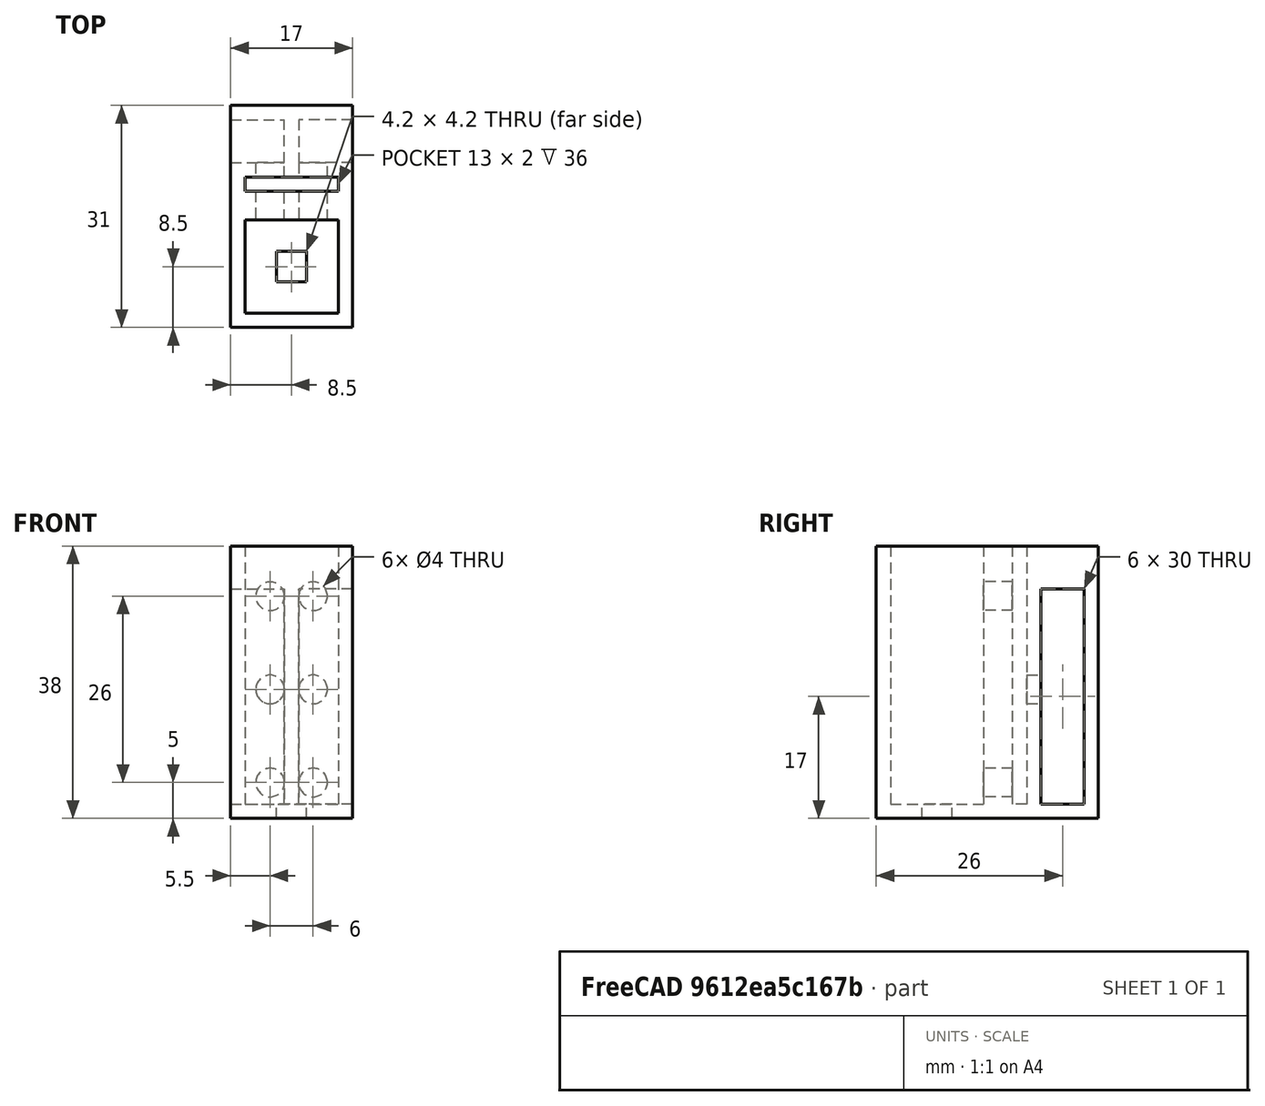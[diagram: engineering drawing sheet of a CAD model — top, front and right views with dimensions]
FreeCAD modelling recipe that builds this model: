
FCSTD DOCUMENT  (FreeCAD 0.18.1R)
Label: CYLINDER
License: All rights reserved
LicenseURL: http://en.wikipedia.org/wiki/All_rights_reserved
objects: TechDraw::DrawViewDimension×12, Sketcher::SketchObject×9, PartDesign::Pocket×7, PartDesign::Plane×6, TechDraw::DrawProjGroupItem×4, TechDraw::DrawSVGTemplate×2, TechDraw::DrawPage×2, PartDesign::Pad×1, PartDesign::Body×1, TechDraw::DrawViewPart×1, TechDraw::DrawProjGroup×1
note: 32 computed .brp shape members not serialized (recipe doc carries the construction recipe); baked Part::Feature solids carry a one-line shape summary decoded from their .brp

FEATURE [Sketcher::SketchObject] Sketch
  MapMode = 5
  Support = -> [XY_Plane]
  sketch-geometry (4):
    g0: LineSegment StartX=0 StartY=31 StartZ=0 EndX=17 EndY=31 EndZ=0
    g1: LineSegment StartX=17 StartY=31 StartZ=0 EndX=17 EndY=0 EndZ=0
    g2: LineSegment StartX=17 StartY=0 StartZ=0 EndX=0 EndY=0 EndZ=0
    g3: LineSegment StartX=0 StartY=0 StartZ=0 EndX=0 EndY=31 EndZ=0
  constraints (11):
    c: Coincident(g0,g1)
    c: Coincident(g1,g2)
    c: Coincident(g2,g3)
    c: Coincident(g3,g0)
    c: Horizontal(g0)
    c: Horizontal(g2)
    c: Vertical(g1)
    c: Vertical(g3)
    c: Coincident(g2,g-1)
    c: DistanceX(g2,g2) = 17
    c: DistanceY(g3,g3) = 31
FEATURE [PartDesign::Pad] Pad
  Length = 38
  Length2 = 100
  Profile = -> Sketch
  Type = 0
FEATURE [PartDesign::Plane] DatumPlane
  Length = 33.6543
  MapMode = 5
  Placement = pos=(0,0,38) rot=(0,0,1;0rad)
  ResizeMode = 0
  Support = -> [Pad]
  Width = 47.6543
FEATURE [Sketcher::SketchObject] Sketch001
  MapMode = 5
  Placement = pos=(0,0,38) rot=(0,0,1;0rad)
  Support = -> [DatumPlane]
  sketch-geometry (4):
    g0: LineSegment StartX=2 StartY=21 StartZ=0 EndX=15 EndY=21 EndZ=0
    g1: LineSegment StartX=15 StartY=21 StartZ=0 EndX=15 EndY=19 EndZ=0
    g2: LineSegment StartX=15 StartY=19 StartZ=0 EndX=2 EndY=19 EndZ=0
    g3: LineSegment StartX=2 StartY=19 StartZ=0 EndX=2 EndY=21 EndZ=0
  constraints (12):
    c: Coincident(g0,g1)
    c: Coincident(g1,g2)
    c: Coincident(g2,g3)
    c: Coincident(g3,g0)
    c: Horizontal(g0)
    c: Horizontal(g2)
    c: Vertical(g1)
    c: Vertical(g3)
    c: DistanceX(g0,g0) = 13
    c: DistanceY(g1,g1) = 2
    c: DistanceX(g-1,g2) = 2
    c: DistanceY(g-1,g0) = 21
FEATURE [Sketcher::SketchObject] Sketch002
  MapMode = 5
  Placement = pos=(0,0,38) rot=(0,0,1;0rad)
  Support = -> [DatumPlane]
  sketch-geometry (4):
    g0: LineSegment StartX=2 StartY=15 StartZ=0 EndX=15 EndY=15 EndZ=0
    g1: LineSegment StartX=15 StartY=15 StartZ=0 EndX=15 EndY=2 EndZ=0
    g2: LineSegment StartX=15 StartY=2 StartZ=0 EndX=2 EndY=2 EndZ=0
    g3: LineSegment StartX=2 StartY=2 StartZ=0 EndX=2 EndY=15 EndZ=0
  constraints (12):
    c: Coincident(g0,g1)
    c: Coincident(g1,g2)
    c: Coincident(g2,g3)
    c: Coincident(g3,g0)
    c: Horizontal(g0)
    c: Horizontal(g2)
    c: Vertical(g1)
    c: Vertical(g3)
    c: DistanceX(g0,g0) = 13
    c: DistanceY(g1,g1) = 13
    c: DistanceX(g-1,g2) = 2
    c: DistanceY(g-1,g0) = 15
FEATURE [PartDesign::Pocket] Pocket001
  BaseFeature = -> Pad
  Length = 36
  Length2 = 100
  Profile = -> Sketch002
  Type = 0
FEATURE [PartDesign::Plane] DatumPlane001
  Length = 33.6543
  MapMode = 5
  Placement = pos=(0,0,0) rot=(1,0,0;3.14159rad)
  ResizeMode = 0
  Support = -> [Pocket001]
  Width = 47.6543
FEATURE [Sketcher::SketchObject] Sketch003
  MapMode = 5
  Placement = pos=(0,0,0) rot=(1,0,0;3.14159rad)
  Support = -> [DatumPlane001]
  sketch-geometry (4):
    g0: LineSegment StartX=6.4 StartY=-6.4 StartZ=0 EndX=10.6 EndY=-6.4 EndZ=0
    g1: LineSegment StartX=10.6 StartY=-6.4 StartZ=0 EndX=10.6 EndY=-10.6 EndZ=0
    g2: LineSegment StartX=10.6 StartY=-10.6 StartZ=0 EndX=6.4 EndY=-10.6 EndZ=0
    g3: LineSegment StartX=6.4 StartY=-10.6 StartZ=0 EndX=6.4 EndY=-6.4 EndZ=0
  constraints (12):
    c: Coincident(g0,g1)
    c: Coincident(g1,g2)
    c: Coincident(g2,g3)
    c: Coincident(g3,g0)
    c: Horizontal(g0)
    c: Horizontal(g2)
    c: Vertical(g1)
    c: Vertical(g3)
    c: DistanceX(g0,g0) = 4.2
    c: Equal(g0,g3)
    c: DistanceY(g0,g-1) = 6.4
    c: DistanceX(g-1,g0) = 6.4
FEATURE [PartDesign::Pocket] Pocket002
  BaseFeature = -> Pocket001
  Length = 5
  Length2 = 100
  Profile = -> Sketch003
  Type = 0
FEATURE [PartDesign::Pocket] Pocket
  BaseFeature = -> Pocket002
  Length = 36
  Length2 = 100
  Profile = -> Sketch001
  Type = 0
FEATURE [PartDesign::Plane] DatumPlane002
  Length = 49.8724
  MapMode = 5
  Placement = pos=(0,0,0) rot=(0.57735,-0.57735,-0.57735;2.0944rad)
  ResizeMode = 0
  Support = -> [Pocket]
  Width = 56.8724
FEATURE [Sketcher::SketchObject] Sketch004
  MapMode = 5
  Placement = pos=(0,0,0) rot=(0.57735,-0.57735,-0.57735;2.0944rad)
  Support = -> [DatumPlane002]
  sketch-geometry (4):
    g0: LineSegment StartX=-29 StartY=32 StartZ=0 EndX=-23 EndY=32 EndZ=0
    g1: LineSegment StartX=-23 StartY=32 StartZ=0 EndX=-23 EndY=2 EndZ=0
    g2: LineSegment StartX=-23 StartY=2 StartZ=0 EndX=-29 EndY=2 EndZ=0
    g3: LineSegment StartX=-29 StartY=2 StartZ=0 EndX=-29 EndY=32 EndZ=0
  constraints (12):
    c: Coincident(g0,g1)
    c: Coincident(g1,g2)
    c: Coincident(g2,g3)
    c: Coincident(g3,g0)
    c: Horizontal(g0)
    c: Horizontal(g2)
    c: Vertical(g1)
    c: Vertical(g3)
    c: DistanceY(g3,g3) = 30
    c: DistanceX(g0,g0) = 6
    c: DistanceX(g1,g-1) = 23
    c: DistanceY(g-1,g2) = 2
FEATURE [Sketcher::SketchObject] Sketch005
  MapMode = 5
  Placement = pos=(0,0,0) rot=(0.57735,-0.57735,-0.57735;2.0944rad)
  Support = -> [DatumPlane002]
FEATURE [PartDesign::Pocket] Pocket003
  BaseFeature = -> Pocket
  Length = 7.5
  Length2 = 100
  Profile = -> Sketch004
  Type = 0
FEATURE [PartDesign::Plane] DatumPlane003
  Length = 49.8724
  MapMode = 5
  Placement = pos=(17,0,0) rot=(0.57735,0.57735,0.57735;2.0944rad)
  ResizeMode = 0
  Support = -> [Pocket003]
  Width = 56.8724
FEATURE [Sketcher::SketchObject] Sketch006
  MapMode = 5
  Placement = pos=(17,0,0) rot=(0.57735,0.57735,0.57735;2.0944rad)
  Support = -> [DatumPlane003]
  sketch-geometry (4):
    g0: LineSegment StartX=23 StartY=32 StartZ=0 EndX=29 EndY=32 EndZ=0
    g1: LineSegment StartX=29 StartY=32 StartZ=0 EndX=29 EndY=2 EndZ=0
    g2: LineSegment StartX=29 StartY=2 StartZ=0 EndX=23 EndY=2 EndZ=0
    g3: LineSegment StartX=23 StartY=2 StartZ=0 EndX=23 EndY=32 EndZ=0
  constraints (12):
    c: Coincident(g0,g1)
    c: Coincident(g1,g2)
    c: Coincident(g2,g3)
    c: Coincident(g3,g0)
    c: Horizontal(g0)
    c: Horizontal(g2)
    c: Vertical(g1)
    c: Vertical(g3)
    c: DistanceY(g1,g1) = 30
    c: DistanceX(g2,g2) = 6
    c: DistanceX(g-1,g2) = 23
    c: DistanceY(g-1,g2) = 2
FEATURE [PartDesign::Pocket] Pocket004
  BaseFeature = -> Pocket003
  Length = 7.5
  Length2 = 100
  Profile = -> Sketch006
  Type = 0
FEATURE [PartDesign::Plane] DatumPlane004
  Length = 34.2
  MapMode = 5
  Placement = pos=(0,15,0) rot=(1,0,0;1.5708rad)
  ResizeMode = 0
  Support = -> [Pocket004]
  Width = 55.2
FEATURE [Sketcher::SketchObject] Sketch007
  MapMode = 5
  Placement = pos=(0,15,0) rot=(1,0,0;1.5708rad)
  Support = -> [DatumPlane004]
  sketch-geometry (4):
    g0: Circle CenterX=5.5 CenterY=31 CenterZ=0 NormalX=0 NormalY=0 NormalZ=1 AngleXU=0 Radius=2
    g1: Circle CenterX=11.5 CenterY=31 CenterZ=0 NormalX=0 NormalY=0 NormalZ=1 AngleXU=0 Radius=2
    g2: Circle CenterX=5.5 CenterY=5 CenterZ=0 NormalX=0 NormalY=0 NormalZ=1 AngleXU=0 Radius=2
    g3: Circle CenterX=11.5 CenterY=5 CenterZ=0 NormalX=0 NormalY=0 NormalZ=1 AngleXU=0 Radius=2
  constraints (12):
    c: Radius(g0) = 2
    c: Radius(g1) = 2
    c: Radius(g2) = 2
    c: Radius(g3) = 2
    c: DistanceX(g0,g1) = 6
    c: DistanceY(g1,g0) = 0
    c: DistanceX(g2,g3) = 6
    c: DistanceY(g3,g2) = 0
    c: DistanceY(g2,g0) = 26
    c: DistanceX(g0,g2) = 0
    c: DistanceY(g-1,g0) = 31
    c: DistanceX(g2,g-1) = -5.5
FEATURE [PartDesign::Pocket] Pocket005
  BaseFeature = -> Pocket004
  Length = 5
  Length2 = 100
  Profile = -> Sketch007
  Type = 0
FEATURE [PartDesign::Plane] DatumPlane005
  Length = 34.2
  MapMode = 5
  Placement = pos=(0,23,0) rot=(0,0.707107,0.707107;3.14159rad)
  ResizeMode = 0
  Support = -> [Pocket005]
  Width = 55.2
FEATURE [Sketcher::SketchObject] Sketch008
  MapMode = 5
  Placement = pos=(0,23,0) rot=(0,0.707107,0.707107;3.14159rad)
  Support = -> [DatumPlane005]
  sketch-geometry (2):
    g0: Circle CenterX=-5.5 CenterY=18 CenterZ=0 NormalX=0 NormalY=0 NormalZ=1 AngleXU=0 Radius=2
    g1: Circle CenterX=-11.5 CenterY=18 CenterZ=0 NormalX=0 NormalY=0 NormalZ=1 AngleXU=0 Radius=2
  constraints (6):
    c: Radius(g0) = 2
    c: Radius(g1) = 2
    c: DistanceX(g1,g0) = 6
    c: DistanceY(g1,g0) = 0
    c: DistanceY(g-1,g1) = 18
    c: DistanceX(g-1,g0) = -5.5
FEATURE [PartDesign::Pocket] Pocket006
  BaseFeature = -> Pocket005
  Length = 2
  Length2 = 100
  Profile = -> Sketch008
  Type = 0
FEATURE [PartDesign::Body] Body
  Group = -> [Sketch,Pad,DatumPlane,Sketch001,Sketch002,Pocket001,DatumPlane001,Sketch003,Pocket002,Pocket,DatumPlane002,Sketch004,Sketch005,Pocket003,DatumPlane003,Sketch006,Pocket004,DatumPlane004,Sketch007,Pocket005,DatumPlane005,Sketch008,Pocket006]
  Origin = -> Origin
  Tip = -> Pocket006
FEATURE [TechDraw::DrawSVGTemplate] Template
  EditableTexts = Designed_by_Name=Designed by Name; Drawing_number=Drawing number; FC-Date=Date; FC-SC=Scale; FC-SH=Sheet; FC-Title=Title; Subtitle=Subtitle; Weight=Weight
  Height = 210
  Orientation = 1
  Width = 297
FEATURE [TechDraw::DrawViewPart] View
  CoarseView = false
  Direction = (0,-1,0)
  Focus = 100
  HardHidden = false
  IsoCount = 0
  IsoHidden = false
  IsoVisible = false
  LockPosition = false
  Perspective = false
  Rotation = 0
  ScaleType = 0
  SeamHidden = false
  SeamVisible = false
  SmoothHidden = false
  SmoothVisible = false
  Source = -> [Body]
  X = 148.5
  Y = 105
FEATURE [TechDraw::DrawPage] Page
  KeepUpdated = true
  ProjectionType = 0
  Template = -> Template
  Views = -> [View]
FEATURE [TechDraw::DrawSVGTemplate] Template001
  EditableTexts = Approved1=Approved 1; Approved2=Approved 2; CheckedBy=Checked By; Code=Code; CompanyAddress=1234 Main St; CompanyName=Company Name; DrawingNumber=Drawing Number; DrawingTitle1=CYLINDER; DrawnBy=Drawn By; Revision=Rev; Scale=Scale; Sheet=Sheet n of m; Weight=Weight
  Height = 279.4
  Orientation = 1
  Width = 431.8
FEATURE [TechDraw::DrawProjGroupItem] ProjItem  label="Front"
  CoarseView = false
  Direction = (0,-1,0)
  Focus = 100
  HardHidden = false
  IsoCount = 0
  IsoHidden = false
  IsoVisible = false
  LockPosition = true
  Perspective = false
  Rotation = 0
  RotationVector = (1,0,0)
  Scale = 2
  ScaleType = 2
  SeamHidden = false
  SeamVisible = false
  SmoothHidden = false
  SmoothVisible = false
  Source = -> [Body]
  Type = 0
  X = 0
  Y = 0
FEATURE [TechDraw::DrawProjGroupItem] ProjItem001  label="Left"
  CoarseView = false
  Direction = (-1,-1e-16,0)
  Focus = 100
  HardHidden = false
  IsoCount = 0
  IsoHidden = false
  IsoVisible = false
  LockPosition = false
  Perspective = false
  Rotation = 0
  RotationVector = (1e-16,-1,0)
  Scale = 2
  ScaleType = 2
  SeamHidden = false
  SeamVisible = false
  SmoothHidden = false
  SmoothVisible = false
  Source = -> [Body]
  Type = 1
  X = 116.246
  Y = 0
FEATURE [TechDraw::DrawProjGroupItem] ProjItem002  label="FrontTopLeft"
  CoarseView = false
  Direction = (-1,-1,1)
  Focus = 100
  HardHidden = false
  IsoCount = 0
  IsoHidden = false
  IsoVisible = false
  LockPosition = false
  Perspective = false
  Rotation = 0
  RotationVector = (1,-1,0)
  Scale = 2
  ScaleType = 2
  SeamHidden = false
  SeamVisible = false
  SmoothHidden = false
  SmoothVisible = false
  Source = -> [Body]
  Type = 6
  X = 116.246
  Y = -116.246
FEATURE [TechDraw::DrawProjGroupItem] ProjItem003  label="Top"
  CoarseView = false
  Direction = (0,0,1)
  Focus = 100
  HardHidden = false
  IsoCount = 0
  IsoHidden = false
  IsoVisible = false
  LockPosition = false
  Perspective = false
  Rotation = 0
  RotationVector = (1,0,0)
  Scale = 2
  ScaleType = 2
  SeamHidden = false
  SeamVisible = false
  SmoothHidden = false
  SmoothVisible = false
  Source = -> [Body]
  Type = 4
  X = 0
  Y = -116.246
FEATURE [TechDraw::DrawProjGroup] ProjGroup
  Anchor = -> ProjItem
  AutoDistribute = true
  LockPosition = false
  ProjectionType = 0
  Rotation = 0
  Scale = 2
  ScaleType = 2
  Source = -> [Body]
  Views = -> [ProjItem,ProjItem001,ProjItem002,ProjItem003]
  X = 83.5356
  Y = 201.47
  spacingX = 15
  spacingY = 15
FEATURE [TechDraw::DrawViewDimension] Dimension
  Arbitrary = false
  FormatSpec = %.4f
  LockPosition = false
  MeasureType = 1
  OverTolerance = 0
  References2D = -> [ProjItem]
  Rotation = 0
  ScaleType = 0
  Type = 1
  UnderTolerance = 0
  X = 2.23762
  Y = 48.2931
FEATURE [TechDraw::DrawViewDimension] Dimension001
  Arbitrary = false
  FormatSpec = %.4f
  LockPosition = false
  MeasureType = 1
  OverTolerance = 0
  References2D = -> [ProjItem]
  Rotation = 0
  ScaleType = 0
  Type = 2
  UnderTolerance = 0
  X = -34.0059
  Y = 2.23762
FEATURE [TechDraw::DrawViewDimension] Dimension002
  Arbitrary = false
  FormatSpec = %.4f
  LockPosition = false
  MeasureType = 1
  OverTolerance = 0
  References2D = -> [ProjItem001]
  Rotation = 0
  ScaleType = 0
  Type = 1
  UnderTolerance = 0
  X = 0.447524
  Y = 47.398
FEATURE [TechDraw::DrawViewDimension] Dimension003
  Arbitrary = false
  FormatSpec = %.4f
  LockPosition = false
  MeasureType = 1
  OverTolerance = 0
  References2D = -> [ProjItem001]
  Rotation = 0
  ScaleType = 0
  Type = 2
  UnderTolerance = 0
  X = 43.0832
  Y = 0
FEATURE [TechDraw::DrawViewDimension] Dimension004
  Arbitrary = false
  FormatSpec = %.4f
  LockPosition = false
  MeasureType = 1
  OverTolerance = 0
  References2D = -> [ProjItem001]
  Rotation = 0
  ScaleType = 0
  Type = 1
  UnderTolerance = 0
  X = -18.3149
  Y = 33.6079
FEATURE [TechDraw::DrawViewDimension] Dimension005
  Arbitrary = false
  FormatSpec = %.4f
  LockPosition = false
  MeasureType = 1
  OverTolerance = 0
  References2D = -> [ProjItem001]
  Rotation = 0
  ScaleType = 0
  Type = 2
  UnderTolerance = 0
  X = -9.62971
  Y = -4.89505
FEATURE [TechDraw::DrawViewDimension] Dimension006
  Arbitrary = false
  FormatSpec = %.4f
  LockPosition = false
  MeasureType = 1
  OverTolerance = 0
  References2D = -> [ProjItem003]
  Rotation = 0
  ScaleType = 0
  Type = 1
  UnderTolerance = 0
  X = -1.7901
  Y = 47.1109
FEATURE [TechDraw::DrawViewDimension] Dimension007
  Arbitrary = false
  FormatSpec = %.4f
  LockPosition = false
  MeasureType = 1
  OverTolerance = 0
  References2D = -> [ProjItem003]
  Rotation = 0
  ScaleType = 0
  Type = 2
  UnderTolerance = 0
  X = 27.2931
  Y = -1.34257
FEATURE [TechDraw::DrawViewDimension] Dimension008
  Arbitrary = false
  FormatSpec = %.4f
  LockPosition = false
  MeasureType = 1
  OverTolerance = 0
  References2D = -> [ProjItem003]
  Rotation = 0
  ScaleType = 0
  Type = 1
  UnderTolerance = 0
  X = -0.447524
  Y = 23.9782
FEATURE [TechDraw::DrawViewDimension] Dimension009
  Arbitrary = false
  FormatSpec = %.4f
  LockPosition = false
  MeasureType = 1
  OverTolerance = 0
  References2D = -> [ProjItem003]
  Rotation = 0
  ScaleType = 0
  Type = 2
  UnderTolerance = 0
  X = 20.1604
  Y = 9.89505
FEATURE [TechDraw::DrawViewDimension] Dimension010
  Arbitrary = false
  FormatSpec = %.4f
  LockPosition = false
  MeasureType = 1
  OverTolerance = 0
  References2D = -> [ProjItem003]
  Rotation = 0
  ScaleType = 0
  Type = 1
  UnderTolerance = 0
  X = 0.447524
  Y = 4.37029
FEATURE [TechDraw::DrawViewDimension] Dimension011
  Arbitrary = false
  FormatSpec = %.4f
  LockPosition = false
  MeasureType = 1
  OverTolerance = 0
  References2D = -> [ProjItem003]
  Rotation = 0
  ScaleType = 0
  Type = 1
  UnderTolerance = 0
  X = 0.895049
  Y = -4.87723
FEATURE [TechDraw::DrawPage] Page001
  KeepUpdated = true
  ProjectionType = 0
  Template = -> Template001
  Views = -> [ProjGroup,Dimension,Dimension001,Dimension002,Dimension003,Dimension004,Dimension005,Dimension006,Dimension007,Dimension008,Dimension009,Dimension010,Dimension011]
